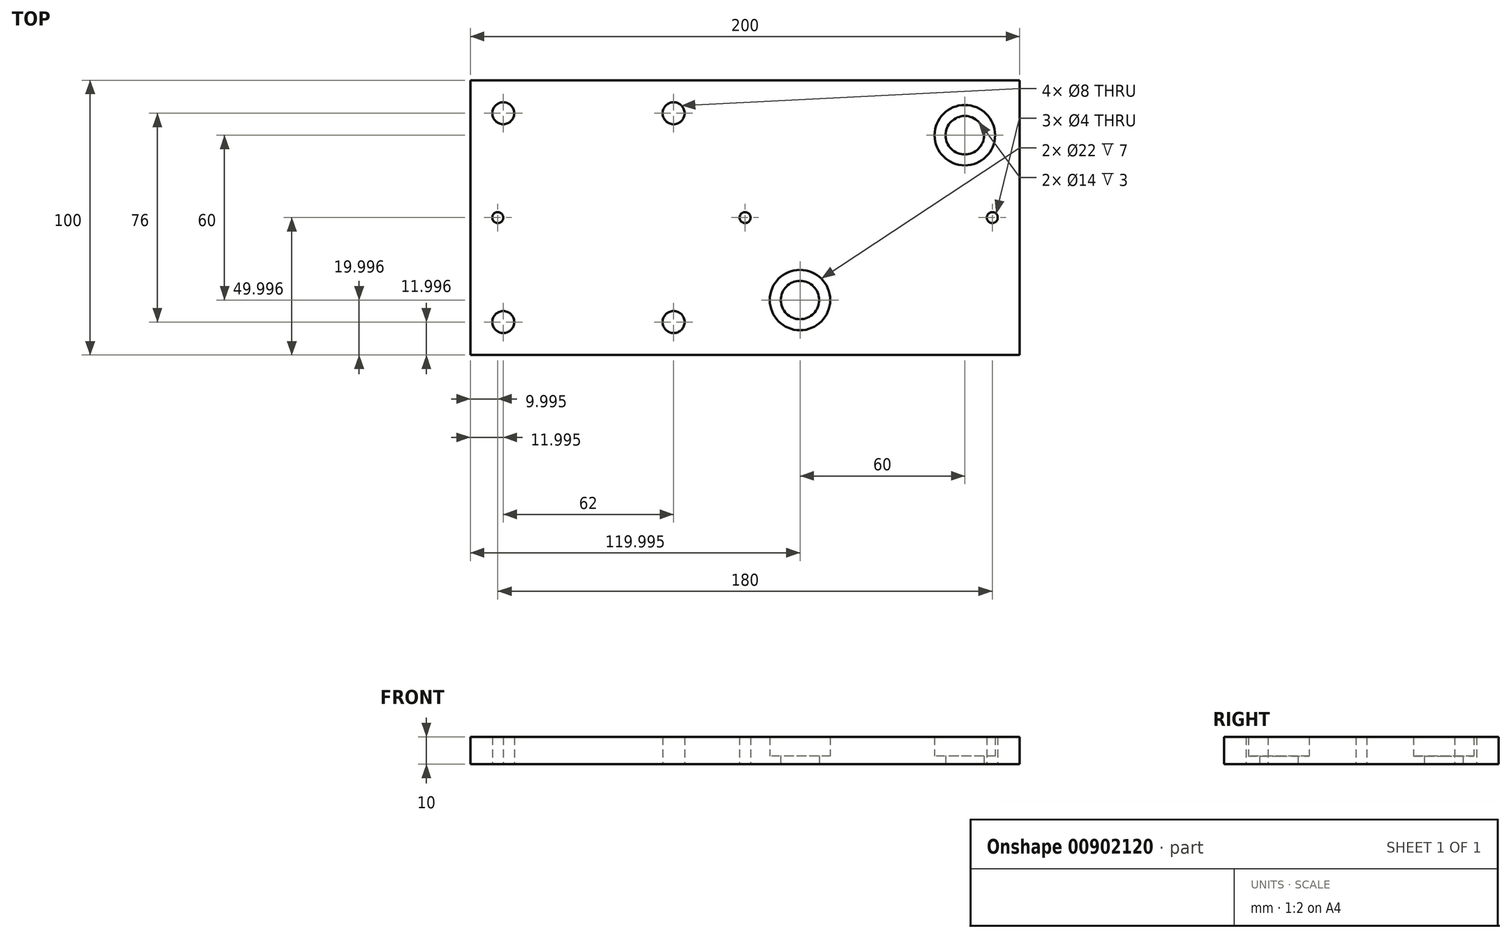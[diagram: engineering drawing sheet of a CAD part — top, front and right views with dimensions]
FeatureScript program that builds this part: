
annotation { "Feature Type Name" : "Feature", "Feature Type Description" : "" }
export const myFeature = defineFeature(function(context is Context, id is Id, definition is map)
    precondition{}
    {
        {
            var Q0;
            Q0=qCreatedBy(makeId("Top.planeOp"),FACE);
            var sketch = newSketch(context, id + "F0", { "sketchPlane" : qUnion([Q0])});
            skLineSegment(sketch, "E0.bottom", {"start": v(-136.01, 62.84) * mm, "end": v(63.99, 62.84) * mm});
            skLineSegment(sketch, "E0.top", {"start": v(-136.01, -37.16) * mm, "end": v(63.99, -37.16) * mm});
            skLineSegment(sketch, "E0.left", {"start": v(-136.01, 62.84) * mm, "end": v(-136.01, -37.16) * mm});
            skLineSegment(sketch, "E0.right", {"start": v(63.99, 62.84) * mm, "end": v(63.99, -37.16) * mm});
            skCircle(sketch, "E1", {"center": v(-124.01, 50.84) * mm, "radius": 4 * mm});
            skCircle(sketch, "E2.MirrorC", {"center": v(-124, -25.16) * mm, "radius": 4 * mm});
            skCircle(sketch, "E3.MirrorC", {"center": v(-62.01, 50.84) * mm, "radius": 4 * mm});
            skCircle(sketch, "E4.MirrorC", {"center": v(-62.01, -25.16) * mm, "radius": 4 * mm});
            skCircle(sketch, "E5", {"center": v(-126.01, 12.84) * mm, "radius": 2 * mm});
            skCircle(sketch, "E6", {"center": v(-36.01, 12.84) * mm, "radius": 2 * mm});
            skCircle(sketch, "E7", {"center": v(53.99, 12.84) * mm, "radius": 2 * mm});
            skCircle(sketch, "E8", {"center": v(-16.01, -17.16) * mm, "radius": 7 * mm});
            skCircle(sketch, "E9", {"center": v(43.99, 42.84) * mm, "radius": 7 * mm});
            skCircle(sketch, "E10", {"center": v(-16.01, -17.16) * mm, "radius": 11 * mm});
            skCircle(sketch, "E11", {"center": v(43.99, 42.84) * mm, "radius": 11 * mm});
            skSolve(sketch);
        }
        {
            var Q0;
            Q0=makeQuery(id+"F0.imprint","IMPRINT",FACE,{"disambiguationData":[TD([[makeQuery(id+"F0.imprint","IMPRINT",EDGE,{"derivedFrom":sQuery(id+"F0.wireOp",EDGE,"E0.bottom")}),-1.0]])]});
            extrude(context, id + "F1", {"entities" : qUnion([Q0]), "depth" : 10 * mm, "offsetDistance" : 25 * mm});
        }
        {
            var Q0;
            Q0=makeQuery(id+"F0.imprint","IMPRINT",FACE,{"disambiguationData":[TD([[makeQuery(id+"F0.imprint","IMPRINT",EDGE,{"derivedFrom":sQuery(id+"F0.wireOp",EDGE,"E8")}),-1.0]])]});
            var Q1;
            Q1=makeQuery(id+"F0.imprint","IMPRINT",FACE,{"disambiguationData":[TD([[makeQuery(id+"F0.imprint","IMPRINT",EDGE,{"derivedFrom":sQuery(id+"F0.wireOp",EDGE,"E9")}),-1.0]])]});
            extrude(context, id + "F2", {"entities" : qUnion([Q0, Q1]), "operationType" : NewBodyOperationType.ADD, "depth" : 3 * mm, "offsetDistance" : 25 * mm});
        }
    });
